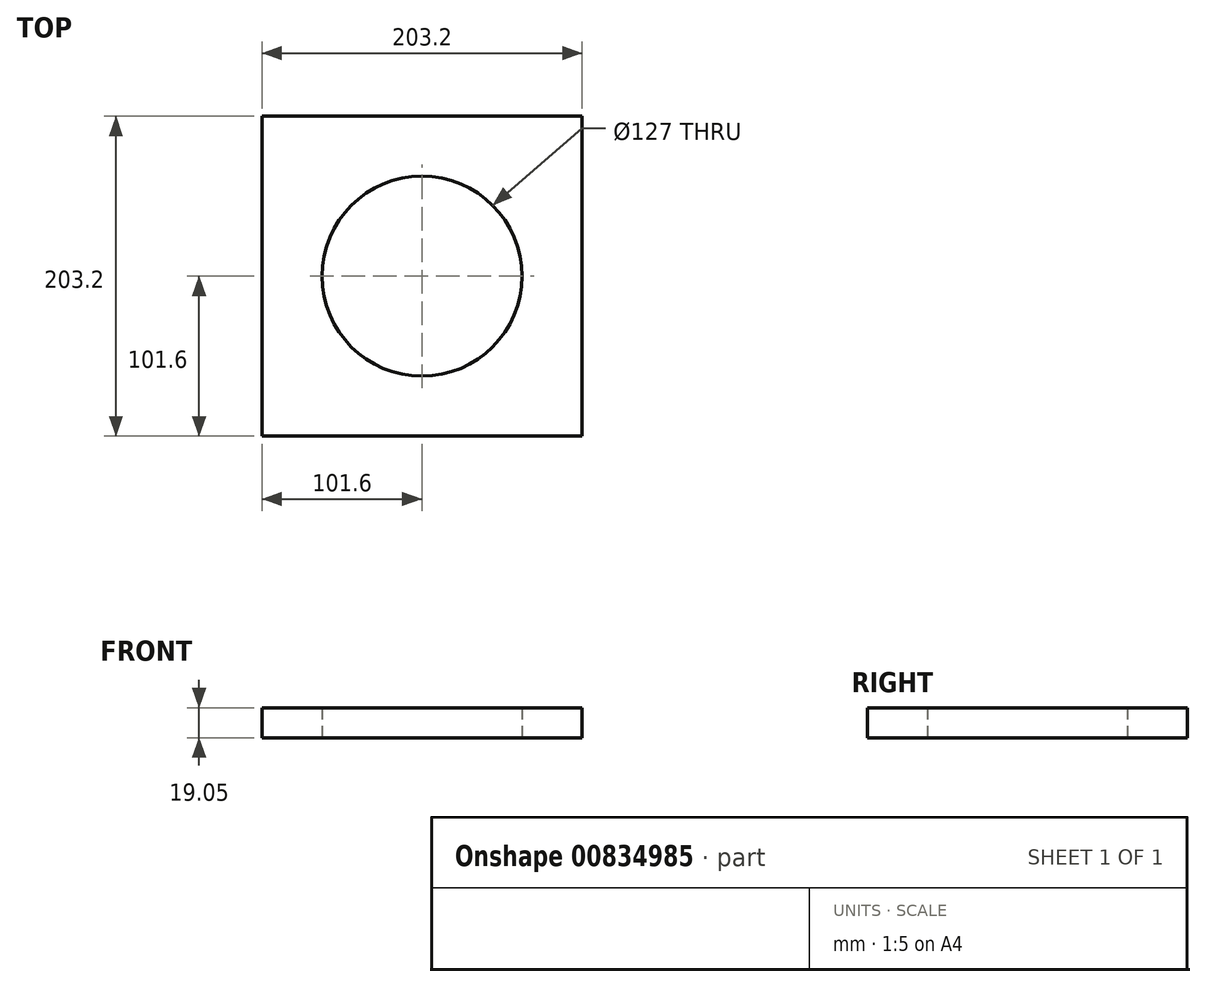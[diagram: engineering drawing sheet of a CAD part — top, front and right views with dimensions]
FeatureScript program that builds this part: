
annotation { "Feature Type Name" : "Feature", "Feature Type Description" : "" }
export const myFeature = defineFeature(function(context is Context, id is Id, definition is map)
    precondition{}
    {
        {
            var Q0;
            Q0=qCreatedBy(makeId("Top.planeOp"),FACE);
            var sketch = newSketch(context, id + "F0", { "sketchPlane" : qUnion([Q0])});
            skLineSegment(sketch, "E0.bottom", {"start": v(-101.6, 101.6) * mm, "end": v(101.6, 101.6) * mm});
            skLineSegment(sketch, "E0.top", {"start": v(-101.6, -101.6) * mm, "end": v(101.6, -101.6) * mm});
            skLineSegment(sketch, "E0.left", {"start": v(-101.6, 101.6) * mm, "end": v(-101.6, -101.6) * mm});
            skLineSegment(sketch, "E0.right", {"start": v(101.6, 101.6) * mm, "end": v(101.6, -101.6) * mm});
            skCircle(sketch, "E1", {"center": v(0, 0) * mm, "radius": 63.5 * mm});
            skSolve(sketch);
        }
        {
            var Q0;
            Q0=makeQuery(id+"F0.imprint","IMPRINT",FACE,{"disambiguationData":[TD([[makeQuery(id+"F0.imprint","IMPRINT",EDGE,{"derivedFrom":sQuery(id+"F0.wireOp",EDGE,"E0.bottom")}),-1.0]])]});
            extrude(context, id + "F1", {"entities" : qUnion([Q0]), "depth" : 19.05 * mm, "offsetDistance" : 25.4 * mm});
        }
    });
